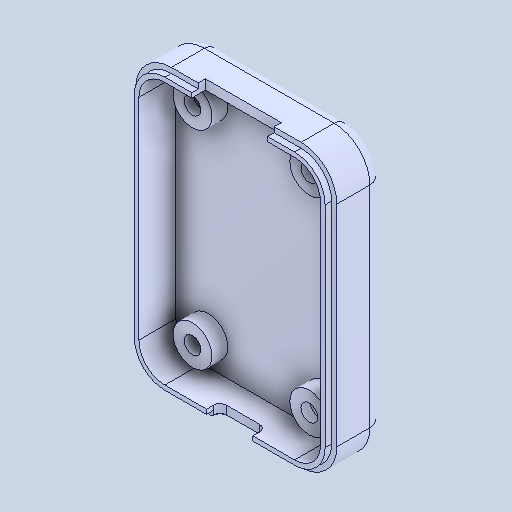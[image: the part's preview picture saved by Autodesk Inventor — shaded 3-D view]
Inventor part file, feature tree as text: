
AUTODESK INVENTOR PART (.ipt)
format: ipt  version: 2022.3 (Build 263350000, 350)  size: 239,616 bytes
history: native  units: in
note: dims shown in document units (in); Inventor stores cm internally (conversion verified against a paired STEP export)
features: fillet x1
ambient origin geometry x8: Origin, YZ Plane, XZ Plane, XY Plane, X Axis, Y Axis, Z Axis, Center Point
bodies: Solid1 (feature_tree)
feature tree (1):
  fillet  "Fillet5"  [1 undecoded]
note: 1 required parameter value undecoded (feature->parameter linkage not recoverable at this tier; creation-order binding heuristic only, values carry confidence <= 0.55)
